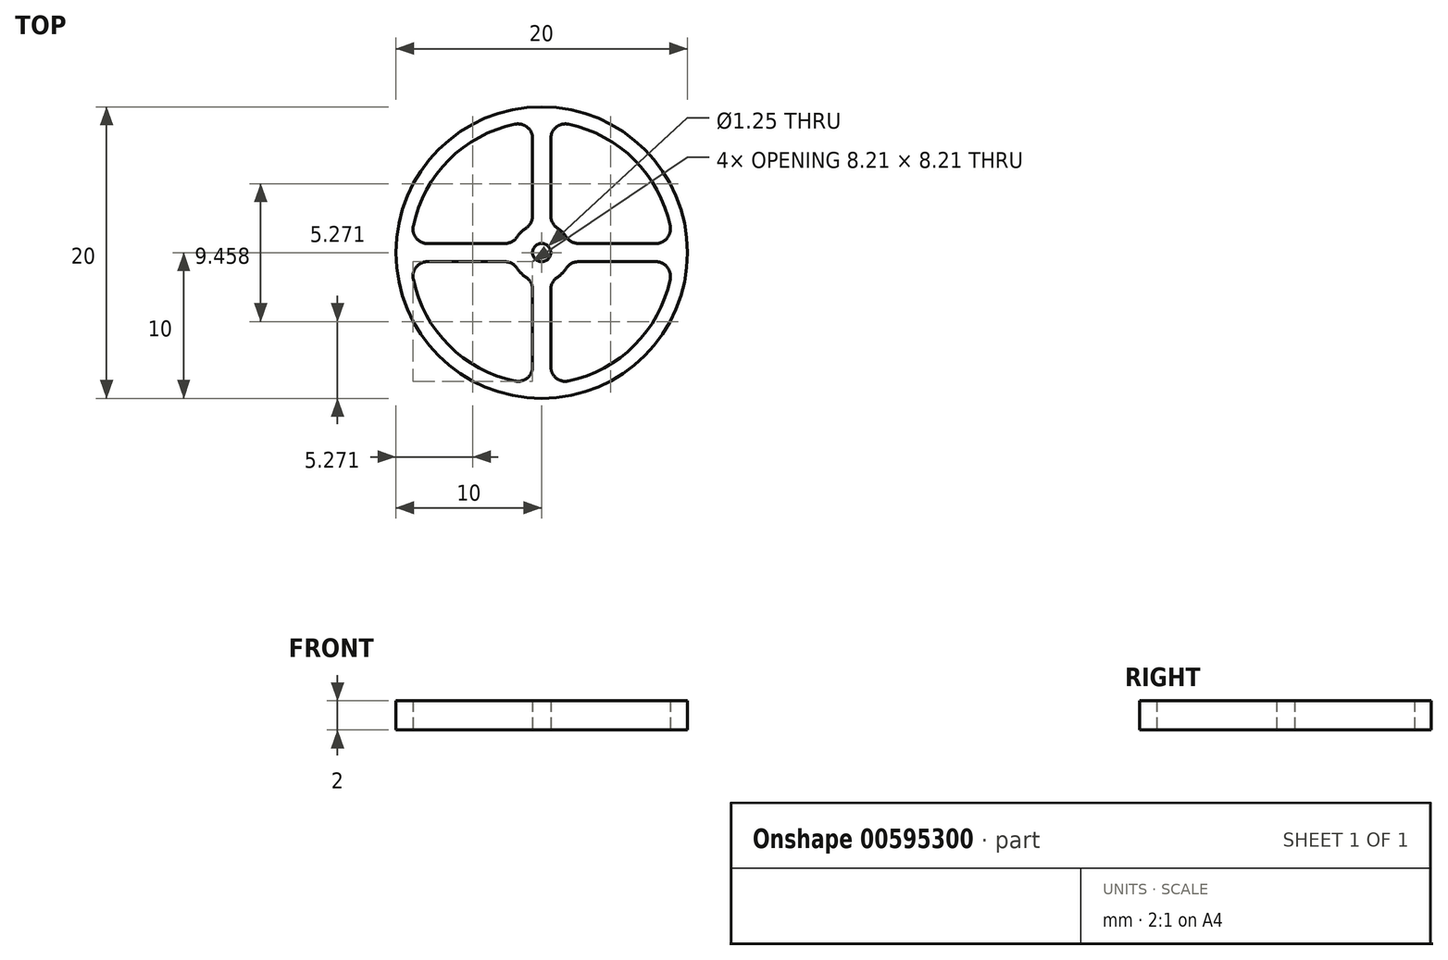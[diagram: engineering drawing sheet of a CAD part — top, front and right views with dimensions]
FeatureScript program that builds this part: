
annotation { "Feature Type Name" : "Feature", "Feature Type Description" : "" }
export const myFeature = defineFeature(function(context is Context, id is Id, definition is map)
    precondition{}
    {
        {
            var Q0;
            Q0=qCreatedBy(makeId("Top.planeOp"),FACE);
            var sketch = newSketch(context, id + "F0", { "sketchPlane" : qUnion([Q0])});
            skArc(sketch, "E0", {"start": v(8.81, 1.83) * mm, "mid": v(6.36, 6.36) * mm, "end": v(1.83, 8.81) * mm});
            skArc(sketch, "E1", {"start": v(1.68, 1.08) * mm, "mid": v(1.41, 1.41) * mm, "end": v(1.08, 1.68) * mm});
            skCircle(sketch, "E2", {"center": v(0, 0) * mm, "radius": 10 * mm});
            skCircle(sketch, "E3", {"center": v(0, 0) * mm, "radius": 0.62 * mm});
            skLineSegment(sketch, "E4.bottom", {"start": v(7.83, -0.62) * mm, "end": v(2.52, -0.62) * mm});
            skLineSegment(sketch, "E4.top", {"start": v(7.83, 0.63) * mm, "end": v(2.52, 0.63) * mm});
            skLineSegment(sketch, "E5.left", {"start": v(0.62, -7.83) * mm, "end": v(0.62, -2.52) * mm});
            skLineSegment(sketch, "E5.right", {"start": v(-0.63, -7.83) * mm, "end": v(-0.63, -2.52) * mm});
            skArc(sketch, "E6.trimOffspring", {"start": v(1.08, -1.68) * mm, "mid": v(1.41, -1.41) * mm, "end": v(1.68, -1.08) * mm});
            skArc(sketch, "E7.trimOffspring", {"start": v(1.83, -8.81) * mm, "mid": v(6.36, -6.36) * mm, "end": v(8.81, -1.83) * mm});
            skArc(sketch, "E8.trimOffspring", {"start": v(-8.81, -1.83) * mm, "mid": v(-6.36, -6.36) * mm, "end": v(-1.83, -8.81) * mm});
            skArc(sketch, "E9.trimOffspring", {"start": v(-1.08, 1.68) * mm, "mid": v(-1.41, 1.41) * mm, "end": v(-1.68, 1.08) * mm});
            skArc(sketch, "E10.trimOffspring", {"start": v(-1.68, -1.08) * mm, "mid": v(-1.41, -1.41) * mm, "end": v(-1.08, -1.68) * mm});
            skLineSegment(sketch, "E11.trimOffspring", {"start": v(-0.62, 2.52) * mm, "end": v(-0.62, 7.83) * mm});
            skLineSegment(sketch, "E12.trimOffspring", {"start": v(0.63, 2.52) * mm, "end": v(0.63, 7.83) * mm});
            skLineSegment(sketch, "E13.trimOffspring", {"start": v(-2.52, -0.63) * mm, "end": v(-7.83, -0.63) * mm});
            skLineSegment(sketch, "E14.trimOffspring", {"start": v(-2.52, 0.62) * mm, "end": v(-7.83, 0.62) * mm});
            skArc(sketch, "E15.trimOffspring", {"start": v(-1.83, 8.81) * mm, "mid": v(-6.36, 6.36) * mm, "end": v(-8.81, 1.83) * mm});
            skPoint(sketch, "E16.visualSharp", {"position": v(0.63, 8.98) * mm});
            skArc(sketch, "E16.filletArc", {"start": v(1.83, 8.81) * mm, "mid": v(1, 8.6) * mm, "end": v(0.63, 7.83) * mm});
            skPoint(sketch, "E17.visualSharp", {"position": v(8.98, 0.63) * mm});
            skArc(sketch, "E17.filletArc", {"start": v(7.83, 0.63) * mm, "mid": v(8.6, 1) * mm, "end": v(8.81, 1.83) * mm});
            skPoint(sketch, "E18.visualSharp", {"position": v(1.9, 0.63) * mm});
            skArc(sketch, "E18.filletArc", {"start": v(1.68, 1.08) * mm, "mid": v(2.04, 0.75) * mm, "end": v(2.52, 0.63) * mm});
            skPoint(sketch, "E19.visualSharp", {"position": v(0.62, 1.9) * mm});
            skArc(sketch, "E19.filletArc", {"start": v(0.63, 2.52) * mm, "mid": v(0.75, 2.04) * mm, "end": v(1.08, 1.68) * mm});
            skPoint(sketch, "E20.visualSharp", {"position": v(-8.98, 0.62) * mm});
            skArc(sketch, "E20.filletArc", {"start": v(-8.81, 1.83) * mm, "mid": v(-8.6, 1) * mm, "end": v(-7.83, 0.62) * mm});
            skPoint(sketch, "E21.visualSharp", {"position": v(-1.9, 0.62) * mm});
            skArc(sketch, "E21.filletArc", {"start": v(-2.52, 0.62) * mm, "mid": v(-2.04, 0.75) * mm, "end": v(-1.68, 1.08) * mm});
            skPoint(sketch, "E22.visualSharp", {"position": v(-0.63, 1.9) * mm});
            skArc(sketch, "E22.filletArc", {"start": v(-1.08, 1.68) * mm, "mid": v(-0.75, 2.04) * mm, "end": v(-0.62, 2.52) * mm});
            skPoint(sketch, "E23.visualSharp", {"position": v(-0.62, 8.98) * mm});
            skArc(sketch, "E23.filletArc", {"start": v(-0.62, 7.83) * mm, "mid": v(-1, 8.6) * mm, "end": v(-1.83, 8.81) * mm});
            skPoint(sketch, "E24.visualSharp", {"position": v(1.9, -0.62) * mm});
            skArc(sketch, "E24.filletArc", {"start": v(2.52, -0.62) * mm, "mid": v(2.04, -0.75) * mm, "end": v(1.68, -1.08) * mm});
            skPoint(sketch, "E25.visualSharp", {"position": v(0.62, -1.9) * mm});
            skArc(sketch, "E25.filletArc", {"start": v(1.08, -1.68) * mm, "mid": v(0.75, -2.04) * mm, "end": v(0.62, -2.52) * mm});
            skPoint(sketch, "E26.visualSharp", {"position": v(0.62, -8.98) * mm});
            skArc(sketch, "E26.filletArc", {"start": v(0.62, -7.83) * mm, "mid": v(1, -8.6) * mm, "end": v(1.83, -8.81) * mm});
            skPoint(sketch, "E27.visualSharp", {"position": v(8.98, -0.62) * mm});
            skArc(sketch, "E27.filletArc", {"start": v(8.81, -1.83) * mm, "mid": v(8.6, -1) * mm, "end": v(7.83, -0.62) * mm});
            skPoint(sketch, "E28.visualSharp", {"position": v(-0.63, -1.9) * mm});
            skArc(sketch, "E28.filletArc", {"start": v(-0.63, -2.52) * mm, "mid": v(-0.75, -2.04) * mm, "end": v(-1.08, -1.68) * mm});
            skPoint(sketch, "E29.visualSharp", {"position": v(-1.9, -0.63) * mm});
            skArc(sketch, "E29.filletArc", {"start": v(-1.68, -1.08) * mm, "mid": v(-2.04, -0.75) * mm, "end": v(-2.52, -0.63) * mm});
            skPoint(sketch, "E30.visualSharp", {"position": v(-8.98, -0.63) * mm});
            skArc(sketch, "E30.filletArc", {"start": v(-7.83, -0.63) * mm, "mid": v(-8.6, -1) * mm, "end": v(-8.81, -1.83) * mm});
            skPoint(sketch, "E31.visualSharp", {"position": v(-0.63, -8.98) * mm});
            skArc(sketch, "E31.filletArc", {"start": v(-1.83, -8.81) * mm, "mid": v(-1, -8.6) * mm, "end": v(-0.63, -7.83) * mm});
            skSolve(sketch);
        }
        {
            var Q0;
            Q0=makeQuery(id+"F0.imprint","IMPRINT",FACE,{"disambiguationData":[TD([[makeQuery(id+"F0.imprint","IMPRINT",EDGE,{"derivedFrom":sQuery(id+"F0.wireOp",EDGE,"E0")}),-1.0]])]});
            extrude(context, id + "F1", {"entities" : qUnion([Q0]), "depth" : 2 * mm, "offsetDistance" : 25 * mm});
        }
    });
